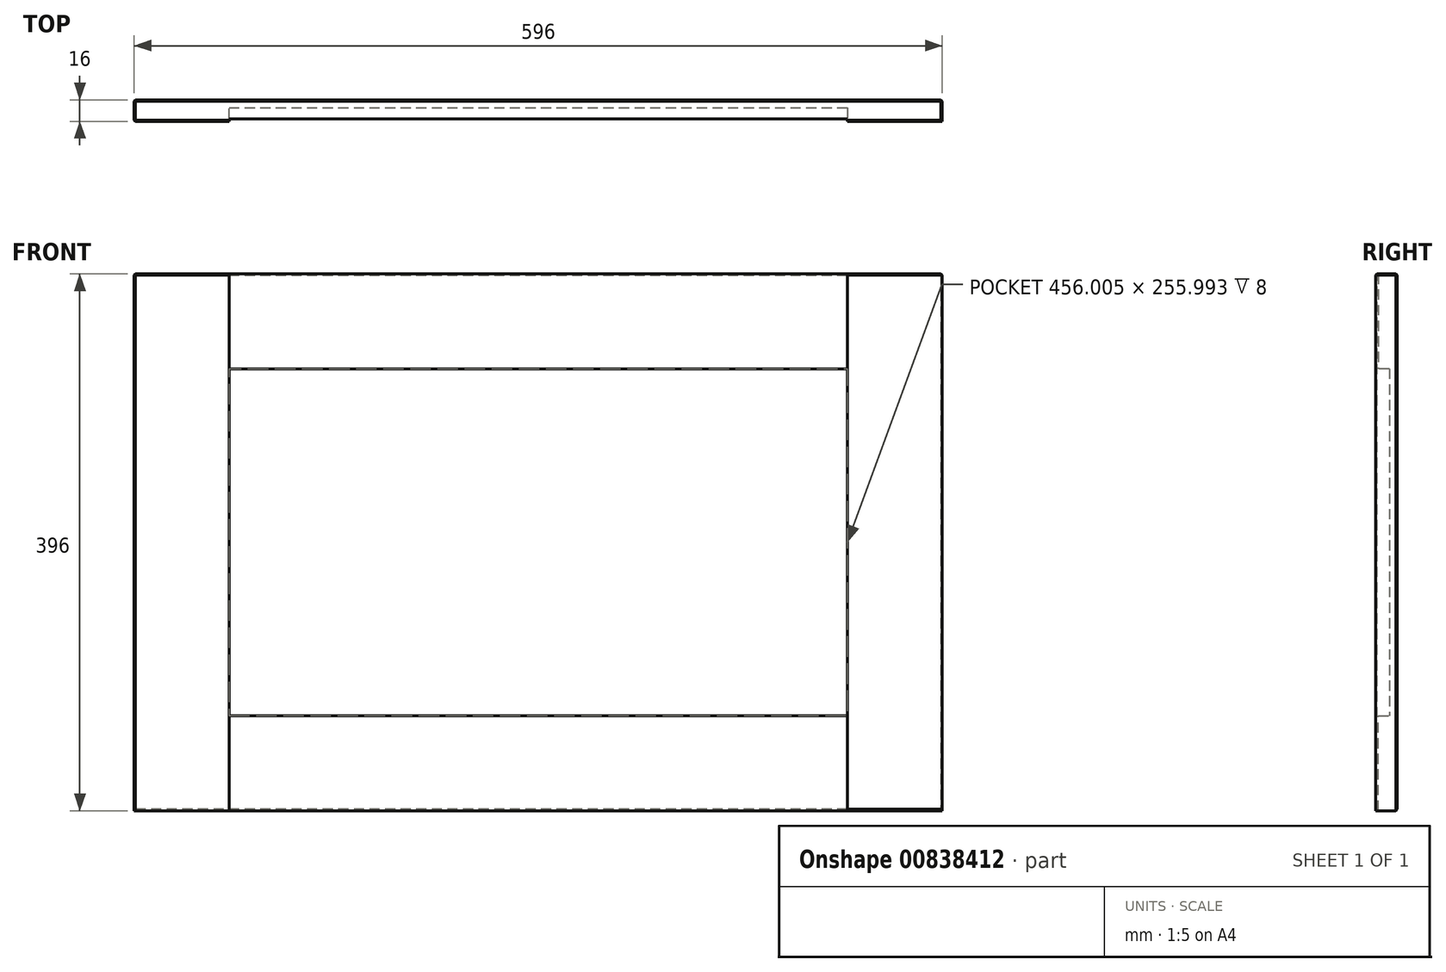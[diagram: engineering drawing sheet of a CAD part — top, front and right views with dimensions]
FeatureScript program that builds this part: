
annotation { "Feature Type Name" : "Feature", "Feature Type Description" : "" }
export const myFeature = defineFeature(function(context is Context, id is Id, definition is map)
    precondition{}
    {
        {
            var Q0;
            Q0=qCreatedBy(makeId("Front.planeOp"),FACE);
            var sketch = newSketch(context, id + "F0", { "sketchPlane" : qUnion([Q0])});
            skLineSegment(sketch, "E0.bottom", {"start": v(0, 0) * mm, "end": v(35.9, 0) * mm});
            skLineSegment(sketch, "E0.top", {"start": v(0, 30.12) * mm, "end": v(35.9, 30.12) * mm});
            skLineSegment(sketch, "E0.left", {"start": v(0, 0) * mm, "end": v(0, 30.12) * mm});
            skLineSegment(sketch, "E0.right", {"start": v(35.9, 0) * mm, "end": v(35.9, 30.12) * mm});
            skSolve(sketch);
        }
        {
            var Q0;
            Q0=makeQuery(id+"F0.imprint","IMPRINT",FACE,{"disambiguationData":[TD([[makeQuery(id+"F0.imprint","IMPRINT",EDGE,{"derivedFrom":sQuery(id+"F0.wireOp",EDGE,"E0.bottom")}),1.0]])]});
            extrude(context, id + "F1", {"entities" : qUnion([Q0]), "depth" : 16 * mm, "offsetDistance" : 25.4 * mm});
        }
        {
            var Q0;
            Q0=makeQuery(id+"F1.opExtrude","SWEPT_FACE",FACE,{"disambiguationData":[OSD([sQuery(id+"F0.wireOp",EDGE,"E0.left")])]});
            extrude(context, id + "F2", {"entities" : qUnion([Q0]), "operationType" : NewBodyOperationType.ADD, "oppositeDirection" : true, "depth" : 196 * mm, "offsetDistance" : 25 * mm});
        }
        {
            var Q0;
            {var subQ0=sQuery(id+"F0.wireOp",EDGE,"E0.bottom");Q0=makeQuery(id+"F2.boolean.opBoolean","MERGE",FACE,{"derivedFrom":[makeQuery(id+"F1.opExtrude","SWEPT_FACE",FACE,{"disambiguationData":[OSD([subQ0])]}),makeQuery(id+"F2.opExtrude","SWEPT_FACE",FACE,{"disambiguationData":[OSD([subQ0,sQuery(id+"F0.wireOp",EDGE,"E0.left")])]})]});}
            extrude(context, id + "F3", {"entities" : qUnion([Q0]), "operationType" : NewBodyOperationType.ADD, "oppositeDirection" : true, "depth" : 796 * mm, "offsetDistance" : 25 * mm});
        }
        {
            var Q0;
            {var subQ0=sQuery(id+"F0.wireOp",EDGE,"E0.left");var subQ1=sQuery(id+"F0.wireOp",EDGE,"E0.bottom");Q0=makeQuery(id+"F3.boolean.opBoolean","MERGE",FACE,{"derivedFrom":[makeQuery(id+"F2.boolean.opBoolean","MERGE",FACE,{"derivedFrom":[makeQuery(id+"F1.opExtrude","CAP_FACE",FACE,{"disambiguationData":[OSD([subQ1,sQuery(id+"F0.wireOp",EDGE,"E0.top"),subQ0,sQuery(id+"F0.wireOp",EDGE,"E0.right")])],"isStart":false}),makeQuery(id+"F2.opExtrude","SWEPT_FACE",FACE,{"disambiguationData":[OSD([subQ0]),TDD([makeQuery(id+"F1.opExtrude","CAP_EDGE",EDGE,{"disambiguationData":[OSD([subQ0])],"isStart":false})])]})]}),makeQuery(id+"F3.opExtrude","SWEPT_FACE",FACE,{"disambiguationData":[OSD([subQ1,subQ0]),TDD([makeQuery(id+"F2.boolean.opBoolean","MERGE",EDGE,{"derivedFrom":[makeQuery(id+"F1.opExtrude","CAP_EDGE",EDGE,{"disambiguationData":[OSD([subQ1])],"isStart":false}),makeQuery(id+"F2.opExtrude","SWEPT_EDGE",EDGE,{"disambiguationData":[OSD([subQ1,subQ0]),TDD([makeQuery(id+"F1.opExtrude","CAP_VERTEX",VERTEX,{"disambiguationData":[OSD([subQ1,subQ0])],"isStart":false})])]})]})])]})]});}
            var sketch = newSketch(context, id + "F4", { "sketchPlane" : qUnion([Q0])});
            skLineSegment(sketch, "E1.bottom", {"start": v(0, 796) * mm, "end": v(42.19, 796) * mm});
            skLineSegment(sketch, "E1.top", {"start": v(0, 751.57) * mm, "end": v(42.19, 751.57) * mm});
            skLineSegment(sketch, "E1.left", {"start": v(0, 796) * mm, "end": v(0, 751.57) * mm});
            skLineSegment(sketch, "E1.right", {"start": v(42.19, 796) * mm, "end": v(42.19, 751.57) * mm});
            skLineSegment(sketch, "E2.bottom", {"start": v(196, 796) * mm, "end": v(153.6, 796) * mm});
            skLineSegment(sketch, "E2.top", {"start": v(196, 746.75) * mm, "end": v(153.6, 746.75) * mm});
            skLineSegment(sketch, "E2.left", {"start": v(196, 796) * mm, "end": v(196, 746.75) * mm});
            skLineSegment(sketch, "E2.right", {"start": v(153.6, 796) * mm, "end": v(153.6, 746.75) * mm});
            skSolve(sketch);
        }
        {
            var Q0;
            Q0=makeQuery(id+"F4.imprint","IMPRINT",FACE,{"disambiguationData":[TD([[makeQuery(id+"F4.imprint","IMPRINT",EDGE,{"derivedFrom":sQuery(id+"F4.wireOp",EDGE,"E1.bottom")}),-1.0]])]});
            var Q1;
            Q1=makeQuery(id+"F4.imprint","IMPRINT",FACE,{"disambiguationData":[TD([[makeQuery(id+"F4.imprint","IMPRINT",EDGE,{"derivedFrom":sQuery(id+"F4.wireOp",EDGE,"E2.bottom")}),-1.0]])]});
            extrude(context, id + "F5", {"entities" : qUnion([Q0, Q1]), "operationType" : NewBodyOperationType.ADD, "depth" : 25 * mm, "offsetDistance" : 25 * mm});
        }
        {
            var Q0;
            {var subQ0=sQuery(id+"F0.wireOp",EDGE,"E0.left");var subQ1=sQuery(id+"F0.wireOp",EDGE,"E0.bottom");Q0=makeQuery(id+"F3.boolean.opBoolean","MERGE",FACE,{"derivedFrom":[makeQuery(id+"F2.boolean.opBoolean","MERGE",FACE,{"derivedFrom":[makeQuery(id+"F1.opExtrude","CAP_FACE",FACE,{"disambiguationData":[OSD([subQ1,sQuery(id+"F0.wireOp",EDGE,"E0.top"),subQ0,sQuery(id+"F0.wireOp",EDGE,"E0.right")])],"isStart":false}),makeQuery(id+"F2.opExtrude","SWEPT_FACE",FACE,{"disambiguationData":[OSD([subQ0]),TDD([makeQuery(id+"F1.opExtrude","CAP_EDGE",EDGE,{"disambiguationData":[OSD([subQ0])],"isStart":false})])]})]}),makeQuery(id+"F3.opExtrude","SWEPT_FACE",FACE,{"disambiguationData":[OSD([subQ1,subQ0]),TDD([makeQuery(id+"F2.boolean.opBoolean","MERGE",EDGE,{"derivedFrom":[makeQuery(id+"F1.opExtrude","CAP_EDGE",EDGE,{"disambiguationData":[OSD([subQ1])],"isStart":false}),makeQuery(id+"F2.opExtrude","SWEPT_EDGE",EDGE,{"disambiguationData":[OSD([subQ1,subQ0]),TDD([makeQuery(id+"F1.opExtrude","CAP_VERTEX",VERTEX,{"disambiguationData":[OSD([subQ1,subQ0])],"isStart":false})])]})]})])]})]});}
            var sketch = newSketch(context, id + "F6", { "sketchPlane" : qUnion([Q0])});
            skLineSegment(sketch, "E3.bottom", {"start": v(196, 0) * mm, "end": v(163.38, 0) * mm});
            skLineSegment(sketch, "E3.top", {"start": v(196, 46.55) * mm, "end": v(163.38, 46.55) * mm});
            skLineSegment(sketch, "E3.left", {"start": v(196, 0) * mm, "end": v(196, 46.55) * mm});
            skLineSegment(sketch, "E3.right", {"start": v(163.38, 0) * mm, "end": v(163.38, 46.55) * mm});
            skLineSegment(sketch, "E4.bottom", {"start": v(0, 0) * mm, "end": v(50.28, 0) * mm});
            skLineSegment(sketch, "E4.top", {"start": v(0, 44.4) * mm, "end": v(50.28, 44.4) * mm});
            skLineSegment(sketch, "E4.left", {"start": v(0, 0) * mm, "end": v(0, 44.4) * mm});
            skLineSegment(sketch, "E4.right", {"start": v(50.28, 0) * mm, "end": v(50.28, 44.4) * mm});
            skSolve(sketch);
        }
        {
            var Q0;
            Q0=makeQuery(id+"F6.imprint","IMPRINT",FACE,{"disambiguationData":[TD([[makeQuery(id+"F6.imprint","IMPRINT",EDGE,{"derivedFrom":sQuery(id+"F6.wireOp",EDGE,"E3.bottom")}),1.0]])]});
            var Q1;
            Q1=makeQuery(id+"F6.imprint","IMPRINT",FACE,{"disambiguationData":[TD([[makeQuery(id+"F6.imprint","IMPRINT",EDGE,{"derivedFrom":sQuery(id+"F6.wireOp",EDGE,"E4.bottom")}),1.0]])]});
            extrude(context, id + "F7", {"entities" : qUnion([Q0, Q1]), "operationType" : NewBodyOperationType.ADD, "depth" : 25 * mm, "offsetDistance" : 25 * mm});
        }
        {
            var Q0;
            Q0=makeQuery(id+"F7.opExtrude","SWEPT_FACE",FACE,{"disambiguationData":[OSD([sQuery(id+"F6.wireOp",EDGE,"E4.right")])]});
            extrude(context, id + "F8", {"entities" : qUnion([Q0]), "operationType" : NewBodyOperationType.ADD, "depth" : 19.72 * mm, "offsetDistance" : 25 * mm});
        }
        {
            var Q0;
            {var subQ0=sQuery(id+"F6.wireOp",EDGE,"E4.top");Q0=makeQuery(id+"F8.boolean.opBoolean","MERGE",FACE,{"derivedFrom":[makeQuery(id+"F7.opExtrude","SWEPT_FACE",FACE,{"disambiguationData":[OSD([subQ0])]}),makeQuery(id+"F8.opExtrude","SWEPT_FACE",FACE,{"disambiguationData":[OSD([subQ0,sQuery(id+"F6.wireOp",EDGE,"E4.right")])]})]});}
            extrude(context, id + "F9", {"entities" : qUnion([Q0]), "operationType" : NewBodyOperationType.ADD, "depth" : 25.6 * mm, "offsetDistance" : 25 * mm});
        }
        {
            var Q0;
            Q0=makeQuery(id+"F7.opExtrude","SWEPT_FACE",FACE,{"disambiguationData":[OSD([sQuery(id+"F6.wireOp",EDGE,"E3.right")])]});
            extrude(context, id + "F10", {"entities" : qUnion([Q0]), "operationType" : NewBodyOperationType.ADD, "depth" : 37.38 * mm, "offsetDistance" : 25 * mm});
        }
        {
            var Q0;
            {var subQ0=sQuery(id+"F6.wireOp",EDGE,"E3.top");Q0=makeQuery(id+"F10.boolean.opBoolean","MERGE",FACE,{"derivedFrom":[makeQuery(id+"F7.opExtrude","SWEPT_FACE",FACE,{"disambiguationData":[OSD([subQ0])]}),makeQuery(id+"F10.opExtrude","SWEPT_FACE",FACE,{"disambiguationData":[OSD([subQ0,sQuery(id+"F6.wireOp",EDGE,"E3.right")])]})]});}
            extrude(context, id + "F11", {"entities" : qUnion([Q0]), "operationType" : NewBodyOperationType.ADD, "depth" : 23.45 * mm, "offsetDistance" : 25 * mm});
        }
        {
            var Q0;
            Q0=makeQuery(id+"F5.opExtrude","SWEPT_FACE",FACE,{"disambiguationData":[OSD([sQuery(id+"F4.wireOp",EDGE,"E1.right")])]});
            extrude(context, id + "F12", {"entities" : qUnion([Q0]), "operationType" : NewBodyOperationType.ADD, "depth" : 27.8 * mm, "offsetDistance" : 25 * mm});
        }
        {
            var Q0;
            {var subQ0=sQuery(id+"F4.wireOp",EDGE,"E1.top");Q0=makeQuery(id+"F12.boolean.opBoolean","MERGE",FACE,{"derivedFrom":[makeQuery(id+"F5.opExtrude","SWEPT_FACE",FACE,{"disambiguationData":[OSD([subQ0])]}),makeQuery(id+"F12.opExtrude","SWEPT_FACE",FACE,{"disambiguationData":[OSD([subQ0,sQuery(id+"F4.wireOp",EDGE,"E1.right")])]})]});}
            extrude(context, id + "F13", {"entities" : qUnion([Q0]), "operationType" : NewBodyOperationType.ADD, "depth" : 25.57 * mm, "offsetDistance" : 25 * mm});
        }
        {
            var Q0;
            Q0=makeQuery(id+"F5.opExtrude","SWEPT_FACE",FACE,{"disambiguationData":[OSD([sQuery(id+"F4.wireOp",EDGE,"E2.top")])]});
            extrude(context, id + "F14", {"entities" : qUnion([Q0]), "operationType" : NewBodyOperationType.ADD, "depth" : 20.75 * mm, "offsetDistance" : 25 * mm});
        }
        {
            var Q0;
            {var subQ0=sQuery(id+"F4.wireOp",EDGE,"E2.right");Q0=makeQuery(id+"F14.boolean.opBoolean","MERGE",FACE,{"derivedFrom":[makeQuery(id+"F5.opExtrude","SWEPT_FACE",FACE,{"disambiguationData":[OSD([subQ0])]}),makeQuery(id+"F14.opExtrude","SWEPT_FACE",FACE,{"disambiguationData":[OSD([sQuery(id+"F4.wireOp",EDGE,"E2.top"),subQ0])]})]});}
            extrude(context, id + "F15", {"entities" : qUnion([Q0]), "operationType" : NewBodyOperationType.ADD, "depth" : 27.6 * mm, "offsetDistance" : 25 * mm});
        }
        {
            var Q0;
            {var subQ0=sQuery(id+"F0.wireOp",EDGE,"E0.left");var subQ1=sQuery(id+"F0.wireOp",EDGE,"E0.bottom");Q0=makeQuery(id+"F3.boolean.opBoolean","MERGE",FACE,{"derivedFrom":[makeQuery(id+"F2.boolean.opBoolean","MERGE",FACE,{"derivedFrom":[makeQuery(id+"F1.opExtrude","CAP_FACE",FACE,{"disambiguationData":[OSD([subQ1,sQuery(id+"F0.wireOp",EDGE,"E0.top"),subQ0,sQuery(id+"F0.wireOp",EDGE,"E0.right")])],"isStart":false}),makeQuery(id+"F2.opExtrude","SWEPT_FACE",FACE,{"disambiguationData":[OSD([subQ0]),TDD([makeQuery(id+"F1.opExtrude","CAP_EDGE",EDGE,{"disambiguationData":[OSD([subQ0])],"isStart":false})])]})]}),makeQuery(id+"F3.opExtrude","SWEPT_FACE",FACE,{"disambiguationData":[OSD([subQ1,subQ0]),TDD([makeQuery(id+"F2.boolean.opBoolean","MERGE",EDGE,{"derivedFrom":[makeQuery(id+"F1.opExtrude","CAP_EDGE",EDGE,{"disambiguationData":[OSD([subQ1])],"isStart":false}),makeQuery(id+"F2.opExtrude","SWEPT_EDGE",EDGE,{"disambiguationData":[OSD([subQ1,subQ0]),TDD([makeQuery(id+"F1.opExtrude","CAP_VERTEX",VERTEX,{"disambiguationData":[OSD([subQ1,subQ0])],"isStart":false})])]})]})])]})]});}
            var sketch = newSketch(context, id + "F16", { "sketchPlane" : qUnion([Q0])});
            skLineSegment(sketch, "E5.bottom", {"start": v(70, 726) * mm, "end": v(126, 726) * mm});
            skLineSegment(sketch, "E5.top", {"start": v(70, 70) * mm, "end": v(126, 70) * mm});
            skLineSegment(sketch, "E5.left", {"start": v(70, 726) * mm, "end": v(70, 70) * mm});
            skLineSegment(sketch, "E5.right", {"start": v(126, 726) * mm, "end": v(126, 70) * mm});
            skSolve(sketch);
        }
        {
            var Q0;
            Q0=makeQuery(id+"F16.imprint","IMPRINT",FACE,{"disambiguationData":[TD([[makeQuery(id+"F16.imprint","IMPRINT",EDGE,{"derivedFrom":sQuery(id+"F16.wireOp",EDGE,"E5.top")}),1.0]])]});
            extrude(context, id + "F17", {"entities" : qUnion([Q0]), "operationType" : NewBodyOperationType.REMOVE, "oppositeDirection" : true, "depth" : 10 * mm, "offsetDistance" : 25 * mm});
        }
        {
            var Q0;
            {var subQ2=sQuery(id+"F0.wireOp",EDGE,"E0.left");var subQ3=sQuery(id+"F0.wireOp",EDGE,"E0.bottom");var subQ4=makeQuery(id+"F1.opExtrude","CAP_FACE",FACE,{"disambiguationData":[OSD([subQ3,sQuery(id+"F0.wireOp",EDGE,"E0.top"),subQ2,sQuery(id+"F0.wireOp",EDGE,"E0.right")])],"isStart":false});var subQ7=makeQuery(id+"F3.opExtrude","SWEPT_FACE",FACE,{"disambiguationData":[OSD([subQ3,subQ2]),TDD([makeQuery(id+"F2.boolean.opBoolean","MERGE",EDGE,{"derivedFrom":[makeQuery(id+"F1.opExtrude","CAP_EDGE",EDGE,{"disambiguationData":[OSD([subQ3])],"isStart":false}),makeQuery(id+"F2.opExtrude","SWEPT_EDGE",EDGE,{"disambiguationData":[OSD([subQ3,subQ2]),TDD([makeQuery(id+"F1.opExtrude","CAP_VERTEX",VERTEX,{"disambiguationData":[OSD([subQ3,subQ2])],"isStart":false})])]})]})])]});var subQ8=makeQuery(id+"F2.opExtrude","SWEPT_FACE",FACE,{"disambiguationData":[OSD([subQ2]),TDD([makeQuery(id+"F1.opExtrude","CAP_EDGE",EDGE,{"disambiguationData":[OSD([subQ2])],"isStart":false})])]});Q0=makeQuery(id+"F17.boolean.opBoolean","SPLIT",FACE,{"disambiguationData":[TD([makeQuery(id+"F1.opExtrude","SWEPT_FACE",FACE,{"disambiguationData":[OSD([subQ3])]})])],"derivedFrom":makeQuery(id+"F3.boolean.opBoolean","MERGE",FACE,{"derivedFrom":[makeQuery(id+"F2.boolean.opBoolean","MERGE",FACE,{"derivedFrom":[subQ4,subQ8]}),subQ7]})});}
            var Q1;
            {var subQ2=sQuery(id+"F4.wireOp",EDGE,"E1.bottom");var subQ3=sQuery(id+"F0.wireOp",EDGE,"E0.left");var subQ4=sQuery(id+"F0.wireOp",EDGE,"E0.bottom");var subQ6=makeQuery(id+"F1.opExtrude","CAP_FACE",FACE,{"disambiguationData":[OSD([subQ4,sQuery(id+"F0.wireOp",EDGE,"E0.top"),subQ3,sQuery(id+"F0.wireOp",EDGE,"E0.right")])],"isStart":false});var subQ7=makeQuery(id+"F2.opExtrude","SWEPT_FACE",FACE,{"disambiguationData":[OSD([subQ3]),TDD([makeQuery(id+"F1.opExtrude","CAP_EDGE",EDGE,{"disambiguationData":[OSD([subQ3])],"isStart":false})])]});var subQ8=makeQuery(id+"F3.opExtrude","SWEPT_FACE",FACE,{"disambiguationData":[OSD([subQ4,subQ3]),TDD([makeQuery(id+"F2.boolean.opBoolean","MERGE",EDGE,{"derivedFrom":[makeQuery(id+"F1.opExtrude","CAP_EDGE",EDGE,{"disambiguationData":[OSD([subQ4])],"isStart":false}),makeQuery(id+"F2.opExtrude","SWEPT_EDGE",EDGE,{"disambiguationData":[OSD([subQ4,subQ3]),TDD([makeQuery(id+"F1.opExtrude","CAP_VERTEX",VERTEX,{"disambiguationData":[OSD([subQ4,subQ3])],"isStart":false})])]})]})])]});Q1=makeQuery(id+"F17.boolean.opBoolean","SPLIT",FACE,{"disambiguationData":[TD([makeQuery(id+"F5.opExtrude","SWEPT_FACE",FACE,{"disambiguationData":[OSD([subQ2])]})])],"derivedFrom":makeQuery(id+"F3.boolean.opBoolean","MERGE",FACE,{"derivedFrom":[makeQuery(id+"F2.boolean.opBoolean","MERGE",FACE,{"derivedFrom":[subQ6,subQ7]}),subQ8]})});}
            extrude(context, id + "F18", {"entities" : qUnion([Q0, Q1]), "operationType" : NewBodyOperationType.REMOVE, "oppositeDirection" : true, "depth" : 2 * mm, "offsetDistance" : 25 * mm});
        }
        {
            var Q0;
            {var subQ0=sQuery(id+"F4.wireOp",EDGE,"E1.right");var subQ1=sQuery(id+"F4.wireOp",EDGE,"E1.top");Q0=makeQuery(id+"F13.boolean.opBoolean","MERGE",FACE,{"derivedFrom":[makeQuery(id+"F12.boolean.opBoolean","MERGE",FACE,{"derivedFrom":[makeQuery(id+"F5.opExtrude","CAP_FACE",FACE,{"disambiguationData":[OSD([sQuery(id+"F4.wireOp",EDGE,"E1.bottom"),subQ1,sQuery(id+"F4.wireOp",EDGE,"E1.left"),subQ0])],"isStart":false}),makeQuery(id+"F12.opExtrude","SWEPT_FACE",FACE,{"disambiguationData":[OSD([subQ0]),TDD([makeQuery(id+"F5.opExtrude","CAP_EDGE",EDGE,{"disambiguationData":[OSD([subQ0])],"isStart":false})])]})]}),makeQuery(id+"F13.opExtrude","SWEPT_FACE",FACE,{"disambiguationData":[OSD([subQ1,subQ0]),TDD([makeQuery(id+"F12.boolean.opBoolean","MERGE",EDGE,{"derivedFrom":[makeQuery(id+"F5.opExtrude","CAP_EDGE",EDGE,{"disambiguationData":[OSD([subQ1])],"isStart":false}),makeQuery(id+"F12.opExtrude","SWEPT_EDGE",EDGE,{"disambiguationData":[OSD([subQ1,subQ0]),TDD([makeQuery(id+"F5.opExtrude","CAP_VERTEX",VERTEX,{"disambiguationData":[OSD([subQ1,subQ0])],"isStart":false})])]})]})])]})]});}
            var Q1;
            {var subQ0=sQuery(id+"F4.wireOp",EDGE,"E2.right");var subQ1=sQuery(id+"F4.wireOp",EDGE,"E2.top");Q1=makeQuery(id+"F15.boolean.opBoolean","MERGE",FACE,{"derivedFrom":[makeQuery(id+"F14.boolean.opBoolean","MERGE",FACE,{"derivedFrom":[makeQuery(id+"F5.opExtrude","CAP_FACE",FACE,{"disambiguationData":[OSD([sQuery(id+"F4.wireOp",EDGE,"E2.bottom"),subQ1,sQuery(id+"F4.wireOp",EDGE,"E2.left"),subQ0])],"isStart":false}),makeQuery(id+"F14.opExtrude","SWEPT_FACE",FACE,{"disambiguationData":[OSD([subQ1]),TDD([makeQuery(id+"F5.opExtrude","CAP_EDGE",EDGE,{"disambiguationData":[OSD([subQ1])],"isStart":false})])]})]}),makeQuery(id+"F15.opExtrude","SWEPT_FACE",FACE,{"disambiguationData":[OSD([subQ1,subQ0]),TDD([makeQuery(id+"F14.boolean.opBoolean","MERGE",EDGE,{"derivedFrom":[makeQuery(id+"F5.opExtrude","CAP_EDGE",EDGE,{"disambiguationData":[OSD([subQ0])],"isStart":false}),makeQuery(id+"F14.opExtrude","SWEPT_EDGE",EDGE,{"disambiguationData":[OSD([subQ1,subQ0]),TDD([makeQuery(id+"F5.opExtrude","CAP_VERTEX",VERTEX,{"disambiguationData":[OSD([subQ1,subQ0])],"isStart":false})])]})]})])]})]});}
            var Q2;
            {var subQ0=sQuery(id+"F6.wireOp",EDGE,"E4.right");var subQ1=sQuery(id+"F6.wireOp",EDGE,"E4.top");Q2=makeQuery(id+"F9.boolean.opBoolean","MERGE",FACE,{"derivedFrom":[makeQuery(id+"F8.boolean.opBoolean","MERGE",FACE,{"derivedFrom":[makeQuery(id+"F7.opExtrude","CAP_FACE",FACE,{"disambiguationData":[OSD([sQuery(id+"F6.wireOp",EDGE,"E4.bottom"),subQ1,sQuery(id+"F6.wireOp",EDGE,"E4.left"),subQ0])],"isStart":false}),makeQuery(id+"F8.opExtrude","SWEPT_FACE",FACE,{"disambiguationData":[OSD([subQ0]),TDD([makeQuery(id+"F7.opExtrude","CAP_EDGE",EDGE,{"disambiguationData":[OSD([subQ0])],"isStart":false})])]})]}),makeQuery(id+"F9.opExtrude","SWEPT_FACE",FACE,{"disambiguationData":[OSD([subQ1,subQ0]),TDD([makeQuery(id+"F8.boolean.opBoolean","MERGE",EDGE,{"derivedFrom":[makeQuery(id+"F7.opExtrude","CAP_EDGE",EDGE,{"disambiguationData":[OSD([subQ1])],"isStart":false}),makeQuery(id+"F8.opExtrude","SWEPT_EDGE",EDGE,{"disambiguationData":[OSD([subQ1,subQ0]),TDD([makeQuery(id+"F7.opExtrude","CAP_VERTEX",VERTEX,{"disambiguationData":[OSD([subQ1,subQ0])],"isStart":false})])]})]})])]})]});}
            var Q3;
            {var subQ0=sQuery(id+"F6.wireOp",EDGE,"E3.right");var subQ1=sQuery(id+"F6.wireOp",EDGE,"E3.top");Q3=makeQuery(id+"F11.boolean.opBoolean","MERGE",FACE,{"derivedFrom":[makeQuery(id+"F10.boolean.opBoolean","MERGE",FACE,{"derivedFrom":[makeQuery(id+"F7.opExtrude","CAP_FACE",FACE,{"disambiguationData":[OSD([sQuery(id+"F6.wireOp",EDGE,"E3.bottom"),subQ1,sQuery(id+"F6.wireOp",EDGE,"E3.left"),subQ0])],"isStart":false}),makeQuery(id+"F10.opExtrude","SWEPT_FACE",FACE,{"disambiguationData":[OSD([subQ0]),TDD([makeQuery(id+"F7.opExtrude","CAP_EDGE",EDGE,{"disambiguationData":[OSD([subQ0])],"isStart":false})])]})]}),makeQuery(id+"F11.opExtrude","SWEPT_FACE",FACE,{"disambiguationData":[OSD([subQ1,subQ0]),TDD([makeQuery(id+"F10.boolean.opBoolean","MERGE",EDGE,{"derivedFrom":[makeQuery(id+"F7.opExtrude","CAP_EDGE",EDGE,{"disambiguationData":[OSD([subQ1])],"isStart":false}),makeQuery(id+"F10.opExtrude","SWEPT_EDGE",EDGE,{"disambiguationData":[OSD([subQ1,subQ0]),TDD([makeQuery(id+"F7.opExtrude","CAP_VERTEX",VERTEX,{"disambiguationData":[OSD([subQ1,subQ0])],"isStart":false})])]})]})])]})]});}
            extrude(context, id + "F19", {"entities" : qUnion([Q0, Q1, Q2, Q3]), "operationType" : NewBodyOperationType.REMOVE, "oppositeDirection" : true, "depth" : 25 * mm, "offsetDistance" : 25 * mm});
        }
        {
            var Q0;
            {var subQ0=sQuery(id+"F4.wireOp",EDGE,"E2.left");var subQ1=sQuery(id+"F0.wireOp",EDGE,"E0.left");var subQ2=sQuery(id+"F0.wireOp",EDGE,"E0.bottom");var subQ3=sQuery(id+"F6.wireOp",EDGE,"E3.left");Q0=makeQuery(id+"F14.boolean.opBoolean","MERGE",FACE,{"derivedFrom":[makeQuery(id+"F11.boolean.opBoolean","MERGE",FACE,{"derivedFrom":[makeQuery(id+"F7.boolean.opBoolean","MERGE",FACE,{"derivedFrom":[makeQuery(id+"F5.boolean.opBoolean","MERGE",FACE,{"derivedFrom":[makeQuery(id+"F3.boolean.opBoolean","MERGE",FACE,{"derivedFrom":[makeQuery(id+"F2.opExtrude","CAP_FACE",FACE,{"disambiguationData":[OSD([subQ1])],"isStart":false}),makeQuery(id+"F3.opExtrude","SWEPT_FACE",FACE,{"disambiguationData":[OSD([subQ2,subQ1]),TDD([makeQuery(id+"F2.opExtrude","CAP_EDGE",EDGE,{"disambiguationData":[OSD([subQ2,subQ1])],"isStart":false})])]})]}),makeQuery(id+"F5.opExtrude","SWEPT_FACE",FACE,{"disambiguationData":[OSD([subQ0])]})]}),makeQuery(id+"F7.opExtrude","SWEPT_FACE",FACE,{"disambiguationData":[OSD([subQ3])]})]}),makeQuery(id+"F11.opExtrude","SWEPT_FACE",FACE,{"disambiguationData":[OSD([subQ2,subQ1,sQuery(id+"F6.wireOp",EDGE,"E3.top"),subQ3])]})]}),makeQuery(id+"F14.opExtrude","SWEPT_FACE",FACE,{"disambiguationData":[OSD([subQ2,subQ1,sQuery(id+"F4.wireOp",EDGE,"E2.top"),subQ0])]})]});}
            extrude(context, id + "F20", {"entities" : qUnion([Q0]), "operationType" : NewBodyOperationType.ADD, "depth" : 200 * mm, "offsetDistance" : 25 * mm});
        }
        {
            var Q0;
            {var subQ0=sQuery(id+"F4.wireOp",EDGE,"E2.right");var subQ1=sQuery(id+"F4.wireOp",EDGE,"E2.top");Q0=makeQuery(id+"F18.boolean.opBoolean","MERGE",FACE,{"derivedFrom":[makeQuery(id+"F15.opExtrude","CAP_FACE",FACE,{"disambiguationData":[OSD([subQ1,subQ0])],"isStart":false}),makeQuery(id+"F18.opExtrude","SWEPT_FACE",FACE,{"disambiguationData":[OSD([subQ1,subQ0])]})]});}
            var Q1;
            {var subQ0=sQuery(id+"F6.wireOp",EDGE,"E3.right");var subQ1=sQuery(id+"F6.wireOp",EDGE,"E3.top");Q1=makeQuery(id+"F18.boolean.opBoolean","MERGE",FACE,{"derivedFrom":[makeQuery(id+"F11.boolean.opBoolean","MERGE",FACE,{"derivedFrom":[makeQuery(id+"F10.opExtrude","CAP_FACE",FACE,{"disambiguationData":[OSD([subQ0])],"isStart":false}),makeQuery(id+"F11.opExtrude","SWEPT_FACE",FACE,{"disambiguationData":[OSD([subQ1,subQ0]),TDD([makeQuery(id+"F10.opExtrude","CAP_EDGE",EDGE,{"disambiguationData":[OSD([subQ1,subQ0])],"isStart":false})])]})]}),makeQuery(id+"F17.boolean.opBoolean","COPY",FACE,{"derivedFrom":makeQuery(id+"F17.opExtrude","SWEPT_FACE",FACE,{"disambiguationData":[OSD([sQuery(id+"F16.wireOp",EDGE,"E5.right")])]})}),makeQuery(id+"F18.opExtrude","SWEPT_FACE",FACE,{"disambiguationData":[OSD([subQ1,subQ0])]})]});}
            extrude(context, id + "F21", {"entities" : qUnion([Q0, Q1]), "operationType" : NewBodyOperationType.REMOVE, "oppositeDirection" : true, "depth" : 200 * mm, "offsetDistance" : 25 * mm});
        }
        {
            var Q0;
            {var subQ0=sQuery(id+"F4.wireOp",EDGE,"E2.bottom");var subQ1=sQuery(id+"F0.wireOp",EDGE,"E0.left");var subQ2=sQuery(id+"F0.wireOp",EDGE,"E0.bottom");var subQ3=sQuery(id+"F4.wireOp",EDGE,"E1.bottom");Q0=makeQuery(id+"F20.boolean.opBoolean","MERGE",FACE,{"derivedFrom":[makeQuery(id+"F15.boolean.opBoolean","MERGE",FACE,{"derivedFrom":[makeQuery(id+"F12.boolean.opBoolean","MERGE",FACE,{"derivedFrom":[makeQuery(id+"F5.boolean.opBoolean","MERGE",FACE,{"derivedFrom":[makeQuery(id+"F3.opExtrude","CAP_FACE",FACE,{"disambiguationData":[OSD([subQ2,subQ1])],"isStart":false}),makeQuery(id+"F5.opExtrude","SWEPT_FACE",FACE,{"disambiguationData":[OSD([subQ3])]}),makeQuery(id+"F5.opExtrude","SWEPT_FACE",FACE,{"disambiguationData":[OSD([subQ0])]})]}),makeQuery(id+"F12.opExtrude","SWEPT_FACE",FACE,{"disambiguationData":[OSD([subQ2,subQ1,subQ3,sQuery(id+"F4.wireOp",EDGE,"E1.right")])]})]}),makeQuery(id+"F15.opExtrude","SWEPT_FACE",FACE,{"disambiguationData":[OSD([subQ2,subQ1,subQ0,sQuery(id+"F4.wireOp",EDGE,"E2.right")])]})]}),makeQuery(id+"F20.opExtrude","SWEPT_FACE",FACE,{"disambiguationData":[OSD([subQ2,subQ1,subQ0,sQuery(id+"F4.wireOp",EDGE,"E2.left")])]})]});}
            extrude(context, id + "F22", {"entities" : qUnion([Q0]), "operationType" : NewBodyOperationType.ADD, "depth" : 200 * mm, "offsetDistance" : 25 * mm});
        }
        {
            var Q0;
            Q0=makeQuery(id+"F17.boolean.opBoolean","COPY",FACE,{"derivedFrom":makeQuery(id+"F17.opExtrude","SWEPT_FACE",FACE,{"disambiguationData":[OSD([sQuery(id+"F16.wireOp",EDGE,"E5.bottom")])]})});
            var Q1;
            {var subQ0=sQuery(id+"F16.wireOp",EDGE,"E5.right");var subQ1=sQuery(id+"F16.wireOp",EDGE,"E5.bottom");var subQ2=sQuery(id+"F4.wireOp",EDGE,"E2.right");var subQ3=sQuery(id+"F4.wireOp",EDGE,"E2.top");var subQ4=makeQuery(id+"F17.boolean.opBoolean","COPY",EDGE,{"derivedFrom":makeQuery(id+"F17.opExtrude","SWEPT_EDGE",EDGE,{"disambiguationData":[OSD([subQ3,subQ2,subQ1,subQ0])]})});Q1=makeQuery(id+"F21.boolean.opBoolean","COPY",FACE,{"derivedFrom":makeQuery(id+"F21.opExtrude","SWEPT_FACE",FACE,{"disambiguationData":[OSD([subQ3,subQ2,subQ1,subQ0]),TDD([makeQuery(id+"F18.boolean.opBoolean","MERGE",EDGE,{"derivedFrom":[subQ4,makeQuery(id+"F18.opExtrude","SWEPT_EDGE",EDGE,{"disambiguationData":[OSD([subQ3,subQ2,subQ1,subQ0])]})]}),makeQuery(id+"F18.boolean.opBoolean","SPLIT",EDGE,{"derivedFrom":subQ4})])]})});}
            extrude(context, id + "F23", {"entities" : qUnion([Q0, Q1]), "operationType" : NewBodyOperationType.REMOVE, "oppositeDirection" : true, "depth" : 200 * mm, "offsetDistance" : 25 * mm});
        }
        {
            var Q0;
            Q0=makeQuery(id+"F23.boolean.opBoolean","COPY",FACE,{"derivedFrom":makeQuery(id+"F23.opExtrude","CAP_FACE",FACE,{"disambiguationData":[OSD([sQuery(id+"F16.wireOp",EDGE,"E5.bottom")])],"isStart":false})});
            var Q1;
            Q1=makeQuery(id+"F23.boolean.opBoolean","COPY",FACE,{"derivedFrom":makeQuery(id+"F23.opExtrude","CAP_FACE",FACE,{"disambiguationData":[OSD([sQuery(id+"F4.wireOp",EDGE,"E2.top"),sQuery(id+"F4.wireOp",EDGE,"E2.right"),sQuery(id+"F16.wireOp",EDGE,"E5.bottom"),sQuery(id+"F16.wireOp",EDGE,"E5.right")])],"isStart":false})});
            extrude(context, id + "F24", {"entities" : qUnion([Q0, Q1]), "operationType" : NewBodyOperationType.ADD, "depth" : 600 * mm, "offsetDistance" : 25 * mm});
        }
        {
            var Q0;
            Q0=makeQuery(id+"F22.opExtrude","CAP_FACE",FACE,{"disambiguationData":[OSD([sQuery(id+"F0.wireOp",EDGE,"E0.bottom"),sQuery(id+"F0.wireOp",EDGE,"E0.left"),sQuery(id+"F4.wireOp",EDGE,"E1.bottom"),sQuery(id+"F4.wireOp",EDGE,"E1.right"),sQuery(id+"F4.wireOp",EDGE,"E2.bottom"),sQuery(id+"F4.wireOp",EDGE,"E2.left"),sQuery(id+"F4.wireOp",EDGE,"E2.right")])],"isStart":false});
            extrude(context, id + "F25", {"entities" : qUnion([Q0]), "operationType" : NewBodyOperationType.REMOVE, "oppositeDirection" : true, "depth" : 600 * mm, "offsetDistance" : 25 * mm, "hasDraft" : true, "draftAngle" : 3 * degree});
        }
        {
            var Q0;
            {var subQ0=sQuery(id+"F4.wireOp",EDGE,"E2.left");var subQ1=sQuery(id+"F0.wireOp",EDGE,"E0.left");var subQ2=sQuery(id+"F0.wireOp",EDGE,"E0.bottom");Q0=makeQuery(id+"F22.boolean.opBoolean","MERGE",FACE,{"derivedFrom":[makeQuery(id+"F20.opExtrude","CAP_FACE",FACE,{"disambiguationData":[OSD([subQ2,subQ1,sQuery(id+"F4.wireOp",EDGE,"E2.top"),subQ0,sQuery(id+"F6.wireOp",EDGE,"E3.top"),sQuery(id+"F6.wireOp",EDGE,"E3.left")])],"isStart":false}),makeQuery(id+"F22.opExtrude","SWEPT_FACE",FACE,{"disambiguationData":[OSD([subQ2,subQ1,sQuery(id+"F4.wireOp",EDGE,"E2.bottom"),subQ0])]})]});}
            extrude(context, id + "F26", {"entities" : qUnion([Q0]), "operationType" : NewBodyOperationType.ADD, "depth" : 200 * mm, "offsetDistance" : 25 * mm, "hasSecondDirection" : true, "secondDirectionOppositeDirection" : true, "secondDirectionDepth" : 25 * mm});
        }
        {
            var Q0;
            {var subQ0=sQuery(id+"F16.wireOp",EDGE,"E5.right");var subQ1=sQuery(id+"F16.wireOp",EDGE,"E5.bottom");var subQ2=sQuery(id+"F4.wireOp",EDGE,"E2.right");var subQ3=sQuery(id+"F4.wireOp",EDGE,"E2.top");var subQ4=makeQuery(id+"F17.boolean.opBoolean","COPY",EDGE,{"derivedFrom":makeQuery(id+"F17.opExtrude","SWEPT_EDGE",EDGE,{"disambiguationData":[OSD([subQ3,subQ2,subQ1,subQ0])]})});Q0=makeQuery(id+"F23.boolean.opBoolean","MERGE",FACE,{"derivedFrom":[makeQuery(id+"F21.boolean.opBoolean","COPY",FACE,{"derivedFrom":makeQuery(id+"F21.opExtrude","CAP_FACE",FACE,{"disambiguationData":[OSD([sQuery(id+"F6.wireOp",EDGE,"E3.top"),sQuery(id+"F6.wireOp",EDGE,"E3.right"),subQ0])],"isStart":false})}),makeQuery(id+"F23.opExtrude","SWEPT_FACE",FACE,{"disambiguationData":[OSD([subQ3,subQ2,subQ1,subQ0]),TDD([makeQuery(id+"F21.boolean.opBoolean","COPY",EDGE,{"derivedFrom":makeQuery(id+"F21.opExtrude","CAP_EDGE",EDGE,{"disambiguationData":[OSD([subQ3,subQ2,subQ1,subQ0]),TDD([makeQuery(id+"F18.boolean.opBoolean","MERGE",EDGE,{"derivedFrom":[subQ4,makeQuery(id+"F18.opExtrude","SWEPT_EDGE",EDGE,{"disambiguationData":[OSD([subQ3,subQ2,subQ1,subQ0])]})]}),makeQuery(id+"F18.boolean.opBoolean","SPLIT",EDGE,{"derivedFrom":subQ4})])],"isStart":false})})])]})]});}
            extrude(context, id + "F27", {"entities" : qUnion([Q0]), "operationType" : NewBodyOperationType.REMOVE, "oppositeDirection" : true, "depth" : 200 * mm, "offsetDistance" : 25 * mm});
        }
        {
            var Q0;
            {var subQ0=sQuery(id+"F4.wireOp",EDGE,"E1.right");var subQ1=sQuery(id+"F4.wireOp",EDGE,"E1.bottom");var subQ2=sQuery(id+"F0.wireOp",EDGE,"E0.left");var subQ3=sQuery(id+"F0.wireOp",EDGE,"E0.bottom");var subQ4=sQuery(id+"F4.wireOp",EDGE,"E1.left");var subQ5=sQuery(id+"F4.wireOp",EDGE,"E1.top");var subQ6=sQuery(id+"F6.wireOp",EDGE,"E4.right");var subQ7=sQuery(id+"F6.wireOp",EDGE,"E4.left");var subQ8=sQuery(id+"F6.wireOp",EDGE,"E4.top");var subQ9=makeQuery(id+"F1.opExtrude","CAP_FACE",FACE,{"disambiguationData":[OSD([subQ3,sQuery(id+"F0.wireOp",EDGE,"E0.top"),subQ2,sQuery(id+"F0.wireOp",EDGE,"E0.right")])],"isStart":false});var subQ10=makeQuery(id+"F3.opExtrude","SWEPT_FACE",FACE,{"disambiguationData":[OSD([subQ3,subQ2]),TDD([makeQuery(id+"F2.boolean.opBoolean","MERGE",EDGE,{"derivedFrom":[makeQuery(id+"F1.opExtrude","CAP_EDGE",EDGE,{"disambiguationData":[OSD([subQ3])],"isStart":false}),makeQuery(id+"F2.opExtrude","SWEPT_EDGE",EDGE,{"disambiguationData":[OSD([subQ3,subQ2]),TDD([makeQuery(id+"F1.opExtrude","CAP_VERTEX",VERTEX,{"disambiguationData":[OSD([subQ3,subQ2])],"isStart":false})])]})]})])]});var subQ11=makeQuery(id+"F2.opExtrude","SWEPT_FACE",FACE,{"disambiguationData":[OSD([subQ2]),TDD([makeQuery(id+"F1.opExtrude","CAP_EDGE",EDGE,{"disambiguationData":[OSD([subQ2])],"isStart":false})])]});Q0=makeQuery(id+"F25.boolean.opBoolean","INTERSECT",EDGE,{"derivedFrom":[makeQuery(id+"F22.boolean.opBoolean","MERGE",FACE,{"derivedFrom":[makeQuery(id+"F19.boolean.opBoolean","MERGE",FACE,{"derivedFrom":[makeQuery(id+"F17.boolean.opBoolean","SPLIT",FACE,{"disambiguationData":[TD([makeQuery(id+"F1.opExtrude","SWEPT_FACE",FACE,{"disambiguationData":[OSD([subQ2])]})])],"derivedFrom":makeQuery(id+"F3.boolean.opBoolean","MERGE",FACE,{"derivedFrom":[makeQuery(id+"F2.boolean.opBoolean","MERGE",FACE,{"derivedFrom":[subQ9,subQ11]}),subQ10]})}),makeQuery(id+"F19.opExtrude","CAP_FACE",FACE,{"disambiguationData":[OSD([sQuery(id+"F6.wireOp",EDGE,"E4.bottom"),subQ8,subQ7,subQ6])],"isStart":false}),makeQuery(id+"F19.opExtrude","CAP_FACE",FACE,{"disambiguationData":[OSD([subQ1,subQ5,subQ4,subQ0])],"isStart":false})]}),makeQuery(id+"F22.opExtrude","SWEPT_FACE",FACE,{"disambiguationData":[OSD([subQ3,subQ2,subQ1,subQ0]),TDD([makeQuery(id+"F19.boolean.opBoolean","COPY",EDGE,{"derivedFrom":makeQuery(id+"F19.opExtrude","CAP_EDGE",EDGE,{"disambiguationData":[OSD([subQ3,subQ2,subQ1,subQ0])],"isStart":false})})])]})]}),makeQuery(id+"F25.opExtrude","CAP_FACE",FACE,{"disambiguationData":[OSD([subQ3,subQ2,subQ1,subQ0,sQuery(id+"F4.wireOp",EDGE,"E2.bottom"),sQuery(id+"F4.wireOp",EDGE,"E2.left"),sQuery(id+"F4.wireOp",EDGE,"E2.right")])],"isStart":false})]});}
            var Q1;
            {var subQ0=sQuery(id+"F4.wireOp",EDGE,"E1.left");var subQ1=sQuery(id+"F0.wireOp",EDGE,"E0.left");var subQ2=sQuery(id+"F0.wireOp",EDGE,"E0.bottom");Q1=makeQuery(id+"F22.boolean.opBoolean","MERGE",EDGE,{"derivedFrom":[makeQuery(id+"F19.boolean.opBoolean","MERGE",EDGE,{"derivedFrom":[makeQuery(id+"F3.boolean.opBoolean","MERGE",EDGE,{"derivedFrom":[makeQuery(id+"F1.opExtrude","CAP_EDGE",EDGE,{"disambiguationData":[OSD([subQ1])],"isStart":false}),makeQuery(id+"F3.opExtrude","SWEPT_EDGE",EDGE,{"disambiguationData":[OSD([subQ2,subQ1]),TDD([makeQuery(id+"F1.opExtrude","CAP_VERTEX",VERTEX,{"disambiguationData":[OSD([subQ2,subQ1])],"isStart":false})])]})]}),makeQuery(id+"F19.opExtrude","CAP_EDGE",EDGE,{"disambiguationData":[OSD([subQ2,subQ1,sQuery(id+"F6.wireOp",EDGE,"E4.top"),sQuery(id+"F6.wireOp",EDGE,"E4.left")])],"isStart":false}),makeQuery(id+"F19.opExtrude","CAP_EDGE",EDGE,{"disambiguationData":[OSD([subQ2,subQ1,sQuery(id+"F4.wireOp",EDGE,"E1.top"),subQ0])],"isStart":false})]}),makeQuery(id+"F22.opExtrude","SWEPT_EDGE",EDGE,{"disambiguationData":[OSD([sQuery(id+"F4.wireOp",EDGE,"E1.bottom"),subQ0])]})]});}
            var Q2;
            Q2=makeQuery(id+"F19.boolean.opBoolean","COPY",EDGE,{"derivedFrom":makeQuery(id+"F19.opExtrude","CAP_EDGE",EDGE,{"disambiguationData":[OSD([sQuery(id+"F0.wireOp",EDGE,"E0.bottom"),sQuery(id+"F0.wireOp",EDGE,"E0.left"),sQuery(id+"F6.wireOp",EDGE,"E4.bottom"),sQuery(id+"F6.wireOp",EDGE,"E4.right")])],"isStart":false})});
            var Q3;
            {var subQ0=sQuery(id+"F6.wireOp",EDGE,"E3.left");var subQ1=sQuery(id+"F6.wireOp",EDGE,"E3.bottom");Q3=makeQuery(id+"F26.boolean.opBoolean","MERGE",EDGE,{"derivedFrom":[makeQuery(id+"F20.boolean.opBoolean","MERGE",EDGE,{"derivedFrom":[makeQuery(id+"F19.boolean.opBoolean","COPY",EDGE,{"derivedFrom":makeQuery(id+"F19.opExtrude","CAP_EDGE",EDGE,{"disambiguationData":[OSD([sQuery(id+"F0.wireOp",EDGE,"E0.bottom"),sQuery(id+"F0.wireOp",EDGE,"E0.left"),subQ1,sQuery(id+"F6.wireOp",EDGE,"E3.right")])],"isStart":false})}),makeQuery(id+"F20.opExtrude","SWEPT_EDGE",EDGE,{"disambiguationData":[OSD([subQ1,subQ0])]})]}),makeQuery(id+"F26.opExtrude","SWEPT_EDGE",EDGE,{"disambiguationData":[OSD([subQ1,subQ0])]})]});}
            var Q4;
            Q4=makeQuery(id+"F26.opExtrude","CAP_EDGE",EDGE,{"disambiguationData":[OSD([sQuery(id+"F0.wireOp",EDGE,"E0.bottom"),sQuery(id+"F0.wireOp",EDGE,"E0.left"),sQuery(id+"F4.wireOp",EDGE,"E2.bottom"),sQuery(id+"F4.wireOp",EDGE,"E2.top"),sQuery(id+"F4.wireOp",EDGE,"E2.left"),sQuery(id+"F6.wireOp",EDGE,"E3.top"),sQuery(id+"F6.wireOp",EDGE,"E3.left")])],"isStart":false});
            var Q5;
            {var subQ0=sQuery(id+"F6.wireOp",EDGE,"E3.right");var subQ1=sQuery(id+"F6.wireOp",EDGE,"E3.left");var subQ2=sQuery(id+"F6.wireOp",EDGE,"E3.top");var subQ3=sQuery(id+"F6.wireOp",EDGE,"E3.bottom");var subQ4=sQuery(id+"F4.wireOp",EDGE,"E2.right");var subQ5=sQuery(id+"F4.wireOp",EDGE,"E2.left");var subQ6=sQuery(id+"F4.wireOp",EDGE,"E2.top");var subQ7=sQuery(id+"F4.wireOp",EDGE,"E2.bottom");var subQ8=sQuery(id+"F4.wireOp",EDGE,"E1.right");var subQ9=sQuery(id+"F4.wireOp",EDGE,"E1.bottom");var subQ10=sQuery(id+"F0.wireOp",EDGE,"E0.right");var subQ11=sQuery(id+"F0.wireOp",EDGE,"E0.left");var subQ12=sQuery(id+"F0.wireOp",EDGE,"E0.top");var subQ13=sQuery(id+"F0.wireOp",EDGE,"E0.bottom");var subQ14=makeQuery(id+"F3.opExtrude","SWEPT_FACE",FACE,{"disambiguationData":[OSD([subQ13,subQ11]),TDD([makeQuery(id+"F2.boolean.opBoolean","MERGE",EDGE,{"derivedFrom":[makeQuery(id+"F1.opExtrude","CAP_EDGE",EDGE,{"disambiguationData":[OSD([subQ13])],"isStart":false}),makeQuery(id+"F2.opExtrude","SWEPT_EDGE",EDGE,{"disambiguationData":[OSD([subQ13,subQ11]),TDD([makeQuery(id+"F1.opExtrude","CAP_VERTEX",VERTEX,{"disambiguationData":[OSD([subQ13,subQ11])],"isStart":false})])]})]})])]});var subQ15=makeQuery(id+"F2.opExtrude","SWEPT_FACE",FACE,{"disambiguationData":[OSD([subQ11]),TDD([makeQuery(id+"F1.opExtrude","CAP_EDGE",EDGE,{"disambiguationData":[OSD([subQ11])],"isStart":false})])]});var subQ16=makeQuery(id+"F1.opExtrude","CAP_FACE",FACE,{"disambiguationData":[OSD([subQ13,subQ12,subQ11,subQ10])],"isStart":false});Q5=makeQuery(id+"F26.boolean.opBoolean","MERGE",EDGE,{"derivedFrom":[makeQuery(id+"F25.boolean.opBoolean","INTERSECT",EDGE,{"derivedFrom":[makeQuery(id+"F22.boolean.opBoolean","MERGE",FACE,{"derivedFrom":[makeQuery(id+"F20.boolean.opBoolean","MERGE",FACE,{"derivedFrom":[makeQuery(id+"F19.boolean.opBoolean","MERGE",FACE,{"derivedFrom":[makeQuery(id+"F17.boolean.opBoolean","SPLIT",FACE,{"disambiguationData":[TD([makeQuery(id+"F2.opExtrude","CAP_FACE",FACE,{"disambiguationData":[OSD([subQ11])],"isStart":false})])],"derivedFrom":makeQuery(id+"F3.boolean.opBoolean","MERGE",FACE,{"derivedFrom":[makeQuery(id+"F2.boolean.opBoolean","MERGE",FACE,{"derivedFrom":[subQ16,subQ15]}),subQ14]})}),makeQuery(id+"F19.opExtrude","CAP_FACE",FACE,{"disambiguationData":[OSD([subQ3,subQ2,subQ1,subQ0])],"isStart":false}),makeQuery(id+"F19.opExtrude","CAP_FACE",FACE,{"disambiguationData":[OSD([subQ7,subQ6,subQ5,subQ4])],"isStart":false})]}),makeQuery(id+"F20.opExtrude","SWEPT_FACE",FACE,{"disambiguationData":[OSD([subQ13,subQ11,subQ6,subQ5,subQ2,subQ1])]})]}),makeQuery(id+"F22.opExtrude","SWEPT_FACE",FACE,{"disambiguationData":[OSD([subQ13,subQ11,subQ7,subQ5,subQ4])]})]}),makeQuery(id+"F25.opExtrude","CAP_FACE",FACE,{"disambiguationData":[OSD([subQ13,subQ11,subQ9,subQ8,subQ7,subQ5,subQ4])],"isStart":false})]}),makeQuery(id+"F26.opExtrude","SWEPT_EDGE",EDGE,{"disambiguationData":[OSD([subQ13,subQ12,subQ11,subQ10,subQ9,subQ8,subQ7,subQ6,subQ5,subQ4,subQ3,subQ2,subQ1,subQ0])]})]});}
            var Q6;
            {var subQ0=sQuery(id+"F0.wireOp",EDGE,"E0.left");var subQ1=sQuery(id+"F0.wireOp",EDGE,"E0.bottom");Q6=makeQuery(id+"F26.boolean.opBoolean","MERGE",FACE,{"derivedFrom":[makeQuery(id+"F22.boolean.opBoolean","MERGE",FACE,{"derivedFrom":[makeQuery(id+"F20.boolean.opBoolean","MERGE",FACE,{"derivedFrom":[makeQuery(id+"F3.boolean.opBoolean","MERGE",FACE,{"derivedFrom":[makeQuery(id+"F2.boolean.opBoolean","MERGE",FACE,{"derivedFrom":[makeQuery(id+"F1.opExtrude","CAP_FACE",FACE,{"disambiguationData":[OSD([subQ1,sQuery(id+"F0.wireOp",EDGE,"E0.top"),subQ0,sQuery(id+"F0.wireOp",EDGE,"E0.right")])],"isStart":true}),makeQuery(id+"F2.opExtrude","SWEPT_FACE",FACE,{"disambiguationData":[OSD([subQ0]),TDD([makeQuery(id+"F1.opExtrude","CAP_EDGE",EDGE,{"disambiguationData":[OSD([subQ0])],"isStart":true})])]})]}),makeQuery(id+"F3.opExtrude","SWEPT_FACE",FACE,{"disambiguationData":[OSD([subQ1,subQ0]),TDD([makeQuery(id+"F2.boolean.opBoolean","MERGE",EDGE,{"derivedFrom":[makeQuery(id+"F1.opExtrude","CAP_EDGE",EDGE,{"disambiguationData":[OSD([subQ1])],"isStart":true}),makeQuery(id+"F2.opExtrude","SWEPT_EDGE",EDGE,{"disambiguationData":[OSD([subQ1,subQ0]),TDD([makeQuery(id+"F1.opExtrude","CAP_VERTEX",VERTEX,{"disambiguationData":[OSD([subQ1,subQ0])],"isStart":true})])]})]})])]})]}),makeQuery(id+"F20.opExtrude","SWEPT_FACE",FACE,{"disambiguationData":[OSD([subQ1,subQ0])]})]}),makeQuery(id+"F22.opExtrude","SWEPT_FACE",FACE,{"disambiguationData":[OSD([subQ1,subQ0])]})]}),makeQuery(id+"F26.opExtrude","SWEPT_FACE",FACE,{"disambiguationData":[OSD([subQ1,subQ0])]})]});}
            chamfer(context, id + "F28", {"entities" : qUnion([Q0, Q1, Q2, Q3, Q4, Q5, Q6]), "width" : 1 * mm, "tangentPropagation" : true});
        }
    });
